# Revit family: Sanitary_Showers_AXOR_26433XXX-AXOR-ShowerSolutions-Ceiling-co22
name_source: partatom
category: Plumbing Fixtures
revit_build: Autodesk Revit 2018 (Build: 20170223_1515(x64)
units: mm (PartAtom-declared; Revit-internal decimal feet)

## family parameters
Always vertical = No
Cut with Voids When Loaded = No
OmniClass Number = 23.31.17.19
OmniClass Title = Shower Head Fixtures
Part Type = Normal
Room Calculation Point = No
Round Connector Dimension = Use Diameter
Shared = No
Work Plane-Based = Yes

## types (1)
- Default - please load Revit Family Type Catalog
    BIMobject category = Showers
    Default Elevation = 1219.2 mm  [stored 4 ft]
    Description = 26433XXX AXOR ShowerSolutions Ceiling connector 300 mm
    Design country = Germany
    EAN code = 4059625030042
    Edition number = 1
    GTIN code = https://4059625030042
    IFC Classification = Sanitary Terminal
    Installation instructions = https://www.axor-design.com
    Manufacturer = AXOR
    Manufacturer country = Germany
    Manufacturer name = AXOR
    Material 1 = AXOR - Metal - 000 Chrome
    Model = 26433XXX
    OmniClass Code = 23-31 17 19
    OmniClass Description = Shower Head Fixtures
    Product Guid = 468cf2a5-bdb7-4fee-965a-668f42ed1d1f
    Product SKU = 26433XXX
    Product data url = https://www.bimobject.com
    Product family = AXOR ShowerSolutions
    Product group = Shower arms
    Product name = 26433XXX AXOR ShowerSolutions Ceiling connector 300 mm
    Product url = https://www.axor-design.com
    QR code = https://www.bimobject.com
    URL = https://www.axor-design.com
    Water Inlet = 13 mm
    Water Inlet Description = Water Inlet 12.7mm
    Weight Net (Kg) = 1,3

note: [stored X ft] marks values corroborated as IEEE doubles in the binary element streams (Revit-internal decimal feet)

## geometry (parser evidence)
native form markers: Sweep x2
no freeform markers — native parametric forms only
